# Revit family: Hager-WITTY PLUS ON PEDESTAL-en-NL
name_source: partatom
category: Electrical Fixtures
units: mm (PartAtom-declared; Revit-internal decimal feet)

## family parameters
Always vertical = Yes
Cut with Voids When Loaded = No
Maintain Annotation Orientation = No
Part Type = Normal
Room Calculation Point = No
Round Connector Dimension = Use Diameter
Shared = No
Work Plane-Based = No

## types (12) — shared parameters
BC_METADATA = {"ObjectGuid":"309c69a2-f6b5-4723-8d44-322179afe64e","ModelGuid":"04826155-e6fb-4358-826f-cf700e871803","VariantGuid":"d0dc6e8a-84e1-41b3-adf0-62c97217fd0d","Revision":"#2","VariantName":"REF 1"}
BC_MODEL_ID = 1528351
BC_OBJECT_ID = 511106
BC_OBJECT_VERSION = #1
Code hager = ADD_EC002883_ECVS_WO
EF000003 - Mounting method = Wall mounting
EF000008 - Width = 250 mm  [stored 0.82021 ft]
EF000040 - Height = 370 mm  [stored 1.21391 ft]
EF000049 - Depth = 150 mm
EF000458 - With display = No
EF001596 - Housing material = Plastic
EF002136 - Nominal connection power = 22000 W
EF003840 - Input voltage = 400 V
EF004293 - Impact strength = IK10
EF005455 - Frequency = 50/60 Hz
EF005474 - Degree of protection (IP) = IP55
EF007001 - Output voltage DC = 0 V
EF007353 - Max. output current DC = 0 A
EF009078 - Number of charging units = 1
EF009089 - With house connection box = No
EF009300 - Max. power per charging point = 22000 W
EF009305 - Number of socket outlets Type 2 = 1
EF009313 - With energy meter = Yes
EF009314 - With miniature circuit breaker (MCB) = No
EF009547 - Long-Term Evolution (LTE) = No
EF011072 - IFTTT support available = No
EF012191 - With built-in RFID card reader = Yes
EF012361 - NFC (Near Field Communication) = No
EF013154 - Networkable via Wi-Fi = Yes
EF014925 - Compatible with Apple HomeKit = No
EF014926 - Compatible with Google Assistant = No
EF014927 - Compatible with Amazon Alexa = No
EF016385 - Mobile communications standard 5G = No
EF017508 - Network-enabled as a master = No
EF017509 - DC residual current detection = No
EF017511 - With key switch = No
EF017512 - Export of charging logs = Yes
EF017513 - OpenChargePointProtocoll (OCPP) version = 1.6
EF017515 - Plug and charge (ISO 15118) = No
EF017517 - Network-enabled as an extender = No
EF017663 - Charging cable permanently lockable at charging device = No
EF017664 - Networkable via LAN = Yes
EF017665 - With MID compliant energy meter = Yes
EF017669 - Suitable for dynamic load management = Yes
EF017672 - Backend included = No
EF017972 - Operation and configuration by app = Yes
EF025053 - Installation side connection model = 3-phase
EFDE0066 - Calibration law compliant = No
ETIM class code = EC002883
ETIM class name = Charging device E-Mobility
HG000003-Range = WITTY PLUS
HG000065-With socket TE = No
HG000099-Onfly Template ID = WittyOne_EVCS_On_Pedestal
Manufacturer = hager France
Name = WITTY PLUS ON PEDESTAL-NL
Name BIM&CO = Electricity
Name hager = ADD_ChargingStation_EC002883
Reference description = ECVS Witty 1x22kW 3P T2S
zero-valued in all types: Default Elevation, EF006577 - Number of CEE socket outlets (IEC 60309), EF008200 - Connectable conductor cross section, EF009091 - Number of earth leakage circuit breakers type A, EF009092 - Number of earth leakage circuit breakers type B, EF009301 - Number of vehicle connectors Type 1, EF009302 - Number of vehicle connectors Type 1 CCS, EF009303 - Number of vehicle connectors Type 2, EF009304 - Number of vehicle connectors Type 2 CCS, EF009306 - Number of vehicle connectors GB AC, EF009307 - Number of vehicle connectors GB DC, EF009308 - Number of socket outlets GB, EF009309 - Number of socket outlets Type 3, EF009310 - Number of vehicle connectors CHAdeMO, EF009311 - Number of household socket outlets

## per-type parameters (varying)
| type | BC_VARIANT_ID | EF014895 - Length of charging cable | EF017668 - Static load management integrated | HG000004-Manufacturer reference |
| WITTY PLUS-1x22kW-3P-XVL122SPI-DOUBLE STATION-RECTANGULAR PEDESTAL | 1164438 | 0 mm  [stored 0 ft] | Yes | XVL122SPI / XVL122SPI / XVA135 |
| WITTY PLUS-1x22kW-3P-XVL122SPI-RECTANGULAR PEDESTAL | 1164439 | 0 mm  [stored 0 ft] | Yes | XVL122SPI / XVA130 |
| WITTY PLUS-1x22kW-3P-XVL122C-RECTANGULAR PEDESTAL | 1164441 | 6500 mm  [stored 21.3255 ft] | No | XVL122C / XVA130 |
| WITTY PLUS-1x22kW-3P-XVL122C-DOUBLE STATION-RECTANGULAR PEDESTAL | 1164444 | 6500 mm  [stored 21.3255 ft] | No | XVL122C / XVL122C / XVA135 |
| WITTY PLUS-1x22kW-3P-XVL122S-RECTANGULAR PEDESTAL | 1164446 | 0 mm  [stored 0 ft] | No | XVL122S / XVA130 |
| WITTY PLUS-1x22kW-3P-XVL122S-DOUBLE STATION-RECTANGULAR PEDESTAL | 1164447 | 0 mm  [stored 0 ft] | No | XVL122S / XVL122S / XVA135 |
| WITTY PLUS-1x22kW-3P-XVL122CPI-RECTANGULAR PEDESTAL | 1164448 | 6500 mm  [stored 21.3255 ft] | Yes | XVL122CPI / XVA130 |
| WITTY PLUS-1x22kW-3P-XVL122CPI-DOUBLE STATION-RECTANGULAR PEDESTAL | 1164449 | 6500 mm  [stored 21.3255 ft] | Yes | XVL122CPI / XVL122CPI / XVA135 |
| WITTY PLUS-1x22kW-3P-XVL122SFL-RECTANGULAR PEDESTAL | 1164450 | 0 mm  [stored 0 ft] | Yes | XVL122SFL / XVA130 |
| WITTY PLUS-1x22kW-3P-XVL122SFL-DOUBLE STATION-RECTANGULAR PEDESTAL | 1164451 | 0 mm  [stored 0 ft] | Yes | XVL122SFL / XVL122SFL / XVA135 |
| WITTY PLUS-1x22kW-3P-XVL122CFL-RECTANGULAR PEDESTAL | 1164452 | 6500 mm  [stored 21.3255 ft] | Yes | XVL122CFL / XVA130 |
| WITTY PLUS-1x22kW-3P-XVL122CFL-DOUBLE STATION-RECTANGULAR PEDESTAL | 1164453 | 6500 mm  [stored 21.3255 ft] | Yes | XVL122CFL / XVL122CFL / XVA135 |

note: column(s) folded — value = type name in every type: Reference

note: [stored X ft] marks values corroborated as IEEE doubles in the binary element streams (Revit-internal decimal feet)
